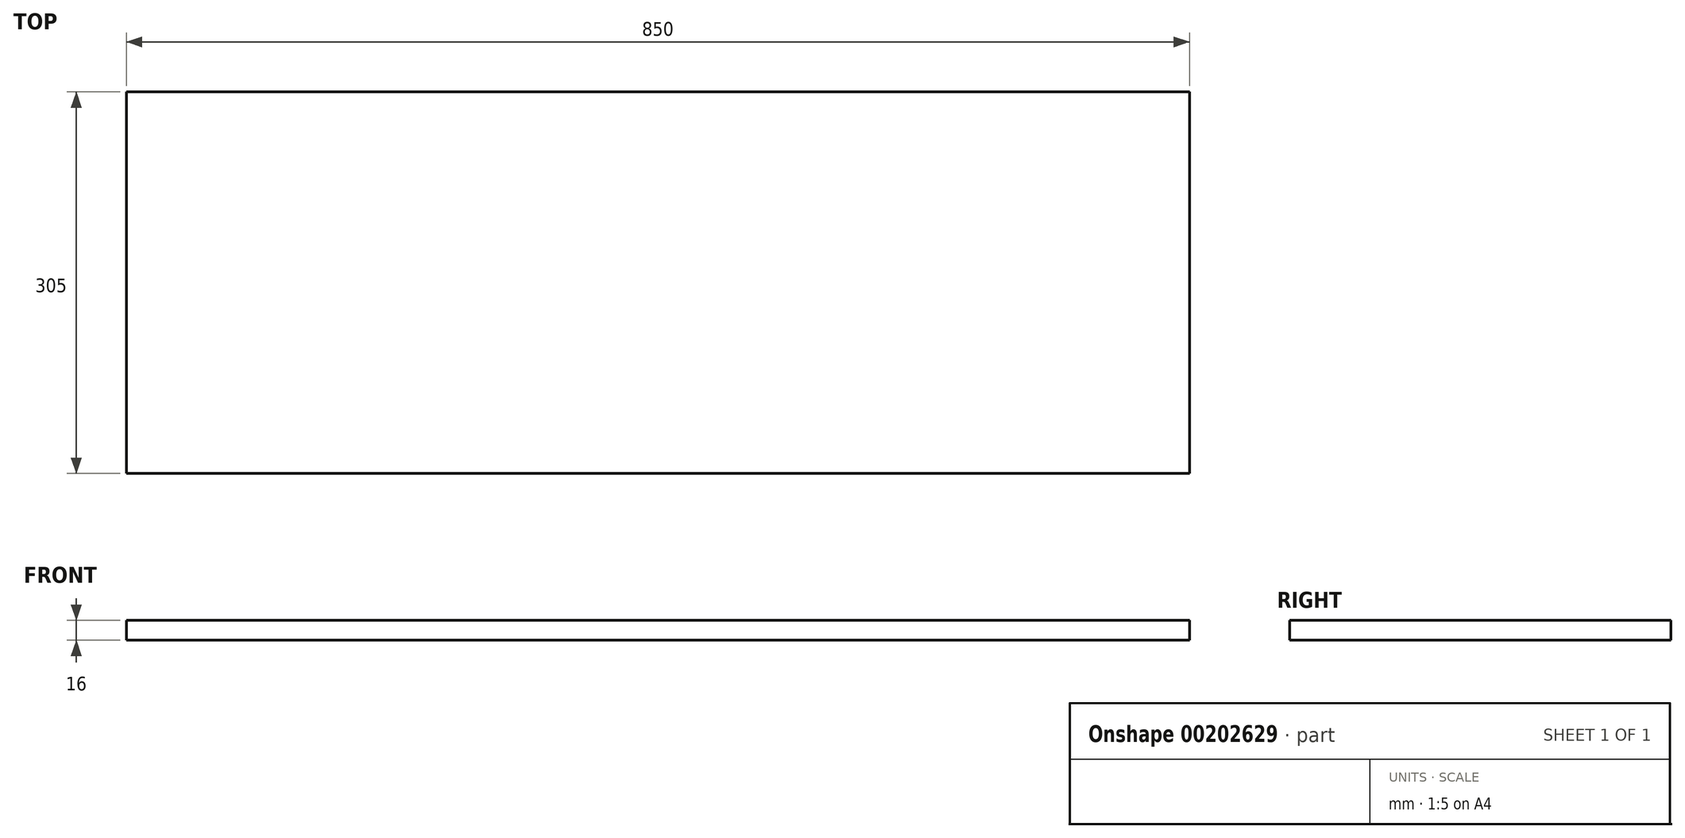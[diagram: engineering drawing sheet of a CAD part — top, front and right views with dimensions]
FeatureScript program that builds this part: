
annotation { "Feature Type Name" : "Feature", "Feature Type Description" : "" }
export const myFeature = defineFeature(function(context is Context, id is Id, definition is map)
    precondition{}
    {
        {
            var Q0;
            Q0=qCreatedBy(makeId("Top.planeOp"),FACE);
            var sketch = newSketch(context, id + "F0", { "sketchPlane" : qUnion([Q0])});
            skLineSegment(sketch, "E0.bottom", {"start": v(-864.34, -235.28) * mm, "end": v(-14.34, -235.28) * mm});
            skLineSegment(sketch, "E0.top", {"start": v(-864.34, 69.72) * mm, "end": v(-14.34, 69.72) * mm});
            skLineSegment(sketch, "E0.left", {"start": v(-864.34, -235.28) * mm, "end": v(-864.34, 69.72) * mm});
            skLineSegment(sketch, "E0.right", {"start": v(-14.34, -235.28) * mm, "end": v(-14.34, 69.72) * mm});
            skSolve(sketch);
        }
        {
            var Q0;
            Q0=makeQuery(id+"F0.imprint","IMPRINT",FACE,{"disambiguationData":[TD([[makeQuery(id+"F0.imprint","IMPRINT",EDGE,{"derivedFrom":sQuery(id+"F0.wireOp",EDGE,"E0.bottom")}),1.0]])]});
            extrude(context, id + "F1", {"entities" : qUnion([Q0]), "depth" : 16 * mm});
        }
    });
